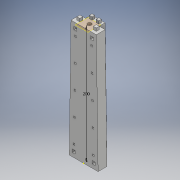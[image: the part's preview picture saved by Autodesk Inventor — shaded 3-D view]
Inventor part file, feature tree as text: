
AUTODESK INVENTOR PART (.ipt)
format: ipt  version: 2017 (Build 210142000, 142)  size: 519,680 bytes
history: native  units: mm
features: sketch x39, extrude x32, chamfer x10, loft x2, plane x1, other x1, hole x1
ambient origin geometry x8: Origin, YZ Plane, XZ Plane, XY Plane, X Axis, Y Axis, Z Axis, Center Point
bodies: Solid1 (feature_tree)
feature tree (86):
  sketch  "Sketch1"  dims[d0=49.0mm d1=15.0mm]
  sketch  "Sketch2"  dims[d2=12.5mm d3=29.0mm]
  sketch  "Sketch3"  dims[d4=10.0mm d5=200.0mm]
  plane  "Work Plane1"
  sketch  "Sketch4"  dims[d6=43.0mm d7=15.0mm]
  sketch  "Sketch5"  dims[d8=12.5mm d9=23.0mm]
  loft  "Loft1"
  loft  "Loft2"
  other  "Work Point1"
  sketch  "Sketch7"  dims[d10=10.0mm d11=0.0mm d12=90.0deg]
  sketch  "Sketch8"  dims[d13=0.0mm d14=90.0deg d15=0.0mm d16=90.0deg]
  sketch  "Sketch11"  dims[d17=0.0mm d18=90.0deg d30=5.5mm]
  sketch  "Sketch12"  dims[d31=5.5mm d32=5.5mm]
  extrude  "Extrusion10"  Depth=200.0mm
  extrude  "Extrusion11"  Depth=15.0mm
  extrude  "Extrusion15"  Depth=23.0mm
  extrude  "Extrusion16"  TaperAngle=0.0deg  [1 undecoded]
  sketch  "Sketch15"  dims[d33=5.5mm d38=4.5mm]
  sketch  "Sketch16"  dims[d39=4.5mm d40=4.5mm]
  sketch  "Sketch18"  dims[d66=6.0mm d67=0.0mm d74=5.0mm d75=0.0mm]
  sketch  "Sketch19"  dims[d76=5.0mm d77=0.0mm d78=2.0mm]
  sketch  "Sketch20"  dims[d79=0.0mm d80=2.0mm]
  extrude  "Extrusion17"  TaperAngle=0.0deg  [1 undecoded]
  extrude  "Extrusion18"  Depth=5.5mm
  extrude  "Extrusion19"  Depth=5.5mm
  extrude  "Extrusion20"  Depth=4.5mm
  extrude  "Extrusion21"  Depth=4.5mm
  extrude  "Extrusion22"  Depth=6.0mm TaperAngle=0.0deg
  extrude  "Extrusion23"  Depth=5.0mm TaperAngle=0.0deg
  extrude  "Extrusion24"  Depth=2.0mm
  extrude  "Extrusion25"  Depth=2.0mm
  extrude  "Extrusion26"  Depth=1.2mm
  extrude  "Extrusion27"  Depth=6.6mm TaperAngle=0.0deg
  extrude  "Extrusion28"  Depth=2.8mm
  extrude  "Extrusion29"  Depth=2.0mm
  extrude  "Extrusion30"  TaperAngle=0.0deg  [1 undecoded]
  extrude  "Extrusion31"  TaperAngle=0.0deg  [1 undecoded]
  extrude  "Extrusion32"  Depth=1.2mm
  extrude  "Extrusion33"  Depth=2.8mm
  extrude  "Extrusion34"  Depth=8.0mm TaperAngle=0.0deg
  extrude  "Extrusion35"  Depth=1.2mm
  extrude  "Extrusion36"  Depth=2.8mm
  chamfer  "Chamfer1"  Distance=8.0mm
  chamfer  "Chamfer2"  Distance=6.6mm
  chamfer  "Chamfer3"  Distance=8.0mm
  chamfer  "Chamfer4"  Distance=6.6mm
  chamfer  "Chamfer5"  Distance=8.0mm
  chamfer  "Chamfer6"  Distance=6.6mm
  chamfer  "Chamfer7"  Distance=2.8mm
  chamfer  "Chamfer8"  Distance=2.8mm
  chamfer  "Chamfer9"  Distance=8.0mm
  chamfer  "Chamfer10"  Distance=2.0mm
  hole  "Hole2"  [1 undecoded]
  sketch  "Sketch37"  dims[d116=2.8mm d117=8.0mm d118=0.0mm]
  sketch  "Sketch38"  dims[d119=1.2mm]
  sketch  "Sketch39"  dims[d120=1.2mm d121=6.6mm d122=0.0mm]
  sketch  "Sketch40"  dims[d123=2.8mm]
  sketch  "Sketch41"  dims[d124=2.8mm d125=8.0mm d126=0.0mm]
  extrude  "Extrusion37"  Depth=1.2mm
  extrude  "Extrusion38"  Depth=1.2mm
  extrude  "Extrusion39"  Depth=6.6mm TaperAngle=0.0deg
  extrude  "Extrusion40"  Depth=2.8mm
  extrude  "Extrusion41"  Depth=2.8mm
  extrude  "Extrusion42"  Depth=8.0mm TaperAngle=0.0deg
  extrude  "Extrusion43"  Depth=2.0mm
  extrude  "Extrusion44"  Depth=1.2mm
  sketch  "Sketch17"  dims[d41=4.5mm d64=6.0mm d65=0.0mm]
  sketch  "Sketch21"  dims[d81=0.0mm d82=1.2mm]
  sketch  "Sketch22"  dims[d83=1.2mm d84=6.6mm d85=0.0mm]
  sketch  "Sketch23"  dims[d86=2.8mm d87=2.8mm]
  sketch  "Sketch24"  dims[d88=8.0mm d89=0.0mm d90=2.0mm]
  sketch  "Sketch26"  dims[d91=2.0mm d92=0.0mm]
  sketch  "Sketch27"  dims[d93=2.0mm d94=0.0mm]
  sketch  "Sketch28"  dims[d95=1.2mm d96=1.2mm]
  sketch  "Sketch29"  dims[d97=6.6mm d98=0.0mm d99=2.8mm]
  sketch  "Sketch30"  dims[d100=2.8mm d101=8.0mm d102=0.0mm]
  sketch  "Sketch31"  dims[d103=1.2mm d104=1.2mm]
  sketch  "Sketch32"  dims[d105=6.6mm d106=0.0mm d107=2.8mm]
  sketch  "Sketch33"  dims[d108=2.8mm d109=8.0mm d110=0.0mm]
  sketch  "Sketch34"  dims[d111=1.2mm]
  sketch  "Sketch35"  dims[d112=1.2mm d113=6.6mm d114=0.0mm]
  sketch  "Sketch36"  dims[d115=2.8mm]
  sketch  "Sketch43"  dims[d127=2.0mm]
  sketch  "Sketch44"  dims[d128=180.0deg]
  sketch  "Sketch45"  dims[d129=1.2mm]
  sketch  "Sketch46"  dims[d130=1.2mm d131=6.6mm d132=0.0mm d133=2.8mm d134=2.8mm d135=8.0mm d136=0.0mm d137=2.0mm d138=180.0deg d139=1.2mm d140=1.2mm d141=6.6mm d142=0.0mm d143=2.8mm d144=2.8mm d145=8.0mm d146=0.0mm d147=2.0mm d148=1.2mm d149=1.2mm d150=6.6mm d151=0.0mm d152=2.8mm d153=2.8mm d154=8.0mm d155=0.0mm d156=2.0mm d157=180.0deg d158=1.2mm d159=1.2mm d160=6.6mm d161=0.0mm d162=2.8mm d163=2.8mm d164=8.0mm d165=0.0mm d166=2.0mm d167=180.0deg d168=1.2mm d169=1.2mm d170=6.6mm d171=0.0mm d172=2.8mm d173=2.8mm d174=8.0mm d175=0.0mm d176=0.8mm d177=2.0mm d178=45.0deg d179=0.8mm d180=2.0mm d181=45.0deg d182=0.8mm d183=2.0mm d184=45.0deg d185=0.8mm d186=2.0mm d187=45.0deg d188=0.8mm d189=2.0mm d190=45.0deg d191=0.73mm d192=2.0mm d193=45.0deg d194=0.7mm d195=2.0mm d196=45.0deg d197=0.8mm d198=2.0mm d199=45.0deg d200=0.7mm d201=2.0mm d202=45.0deg d203=0.7mm d204=2.0mm d205=45.0deg d206=15.0mm d207=6.4mm d208=6.0mm d209=4.0mm d210=2.0mm d211=90.0deg d212=8.0mm d213=20.594885mm d214=7.5mm d215=9.0mm d216=5.0mm d217=5.0mm d218=7.5mm d219=9.0mm d220=5.0mm d221=5.0mm d222=7.5mm d223=9.0mm d224=5.0mm d225=5.0mm d226=7.5mm d227=9.0mm d228=5.0mm d229=5.0mm d230=6.0mm d231=0.0mm d232=6.0mm d233=0.0mm d234=6.0mm d235=0.0mm d236=6.0mm d237=0.0mm d238=5.0mm d239=5.0mm d240=5.0mm d241=5.0mm d242=5.0mm d243=0.0mm d244=5.0mm d245=5.0mm d246=5.0mm d247=5.0mm d248=5.0mm d249=0.0mm d250=4.75mm d251=4.75mm d252=5.5mm d253=5.5mm d254=6.0mm d255=0.0mm d256=4.75mm d257=4.75mm d258=5.5mm d259=5.5mm d260=6.0mm d261=0.0mm]
note: 5 required parameter values undecoded (feature->parameter linkage not recoverable at this tier; creation-order binding heuristic only, values carry confidence <= 0.55)
